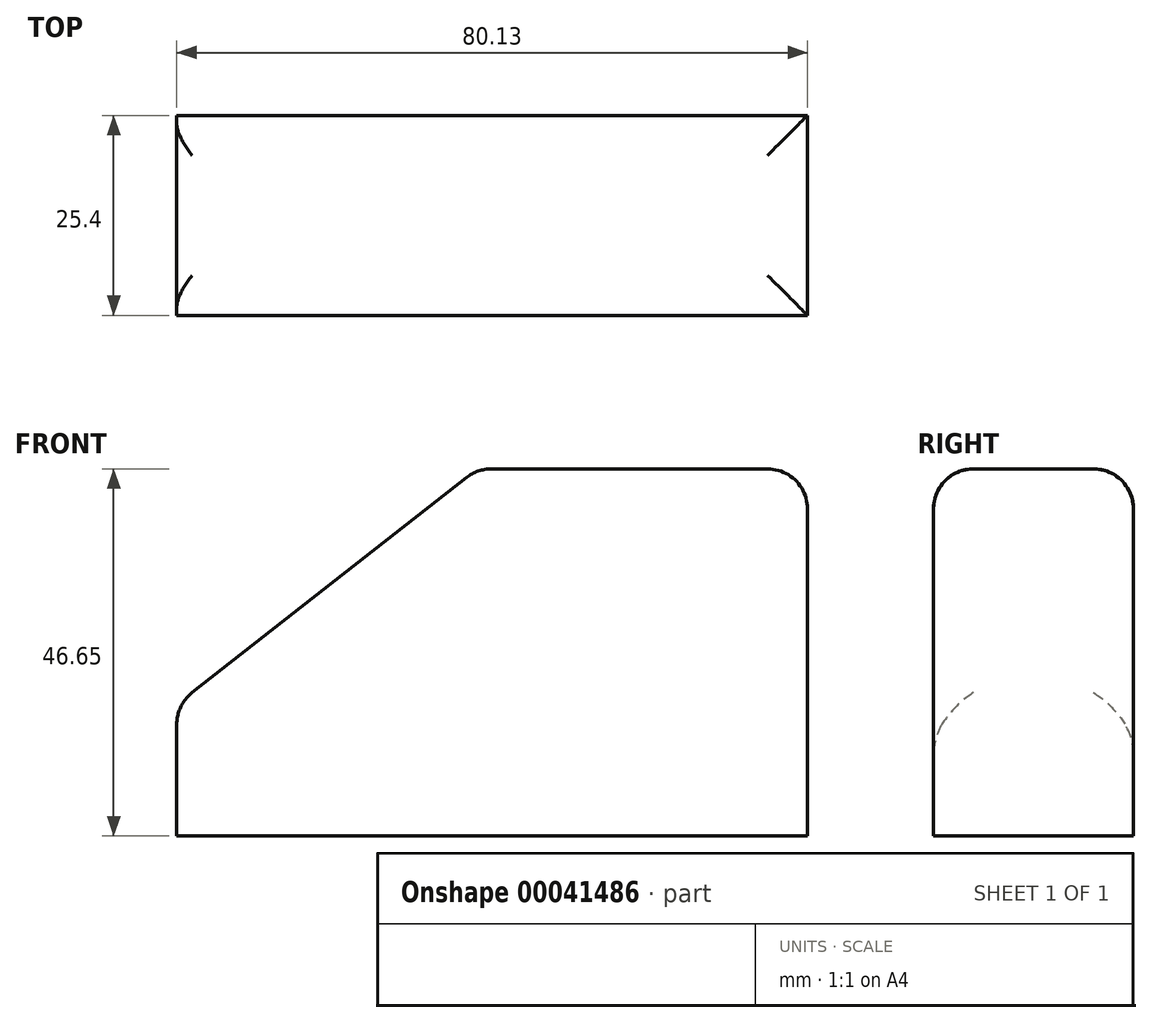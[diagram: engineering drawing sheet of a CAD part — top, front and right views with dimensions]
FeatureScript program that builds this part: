
annotation { "Feature Type Name" : "Feature", "Feature Type Description" : "" }
export const myFeature = defineFeature(function(context is Context, id is Id, definition is map)
    precondition{}
    {
        {
            var Q0;
            Q0=qCreatedBy(makeId("Front.planeOp"),FACE);
            var sketch = newSketch(context, id + "F0", { "sketchPlane" : qUnion([Q0])});
            skLineSegment(sketch, "E0", {"start": v(-44.8, -9.58) * mm, "end": v(19.4, 40.76) * mm});
            skLineSegment(sketch, "E1.bottom", {"start": v(-34.4, 28.52) * mm, "end": v(45.72, 28.52) * mm});
            skLineSegment(sketch, "E1.top", {"start": v(-34.4, -18.13) * mm, "end": v(45.72, -18.13) * mm});
            skLineSegment(sketch, "E1.left", {"start": v(-34.4, 28.52) * mm, "end": v(-34.4, -18.13) * mm});
            skLineSegment(sketch, "E1.right", {"start": v(45.72, 28.52) * mm, "end": v(45.72, -18.13) * mm});
            skLineSegment(sketch, "E2.bottom", {"start": v(-34.4, 28.52) * mm, "end": v(-53.57, 28.52) * mm});
            skLineSegment(sketch, "E2.top", {"start": v(-34.4, 42.6) * mm, "end": v(-53.57, 42.6) * mm});
            skLineSegment(sketch, "E2.left", {"start": v(-34.4, 28.52) * mm, "end": v(-34.4, 42.6) * mm});
            skLineSegment(sketch, "E2.right", {"start": v(-53.57, 28.52) * mm, "end": v(-53.57, 42.6) * mm});
            skSolve(sketch);
        }
        {
            var Q0;
            {var subQ6=sQuery(id+"F0.wireOp",EDGE,"E1.top");Q0=makeQuery(id+"F0.imprint","IMPRINT",FACE,{"disambiguationData":[TD([[makeQuery(id+"F0.imprint","IMPRINT",EDGE,{"derivedFrom":subQ6}),1.0]])]});}
            extrude(context, id + "F1", {"entities" : qUnion([Q0]), "depth" : 25.4 * mm});
        }
        {
            var Q0;
            Q0=makeQuery(id+"F1.opExtrude","SWEPT_FACE",FACE,{"disambiguationData":[OSD([sQuery(id+"F0.wireOp",EDGE,"E1.bottom")])]});
            var Q1;
            Q1=makeQuery(id+"F1.opExtrude","SWEPT_FACE",FACE,{"disambiguationData":[OSD([sQuery(id+"F0.wireOp",EDGE,"E0")])]});
            var Q2;
            Q2=makeQuery(id+"F1.opExtrude","SWEPT_EDGE",EDGE,{"disambiguationData":[OSD([sQuery(id+"F0.wireOp",EDGE,"E0"),sQuery(id+"F0.wireOp",EDGE,"E1.bottom")])]});
            fillet(context, id + "F2", {"entities" : qUnion([Q0, Q1, Q2]), "radius" : 5.08 * mm, "tangentPropagation" : true, "allowEdgeOverflow" : false});
        }
    });
